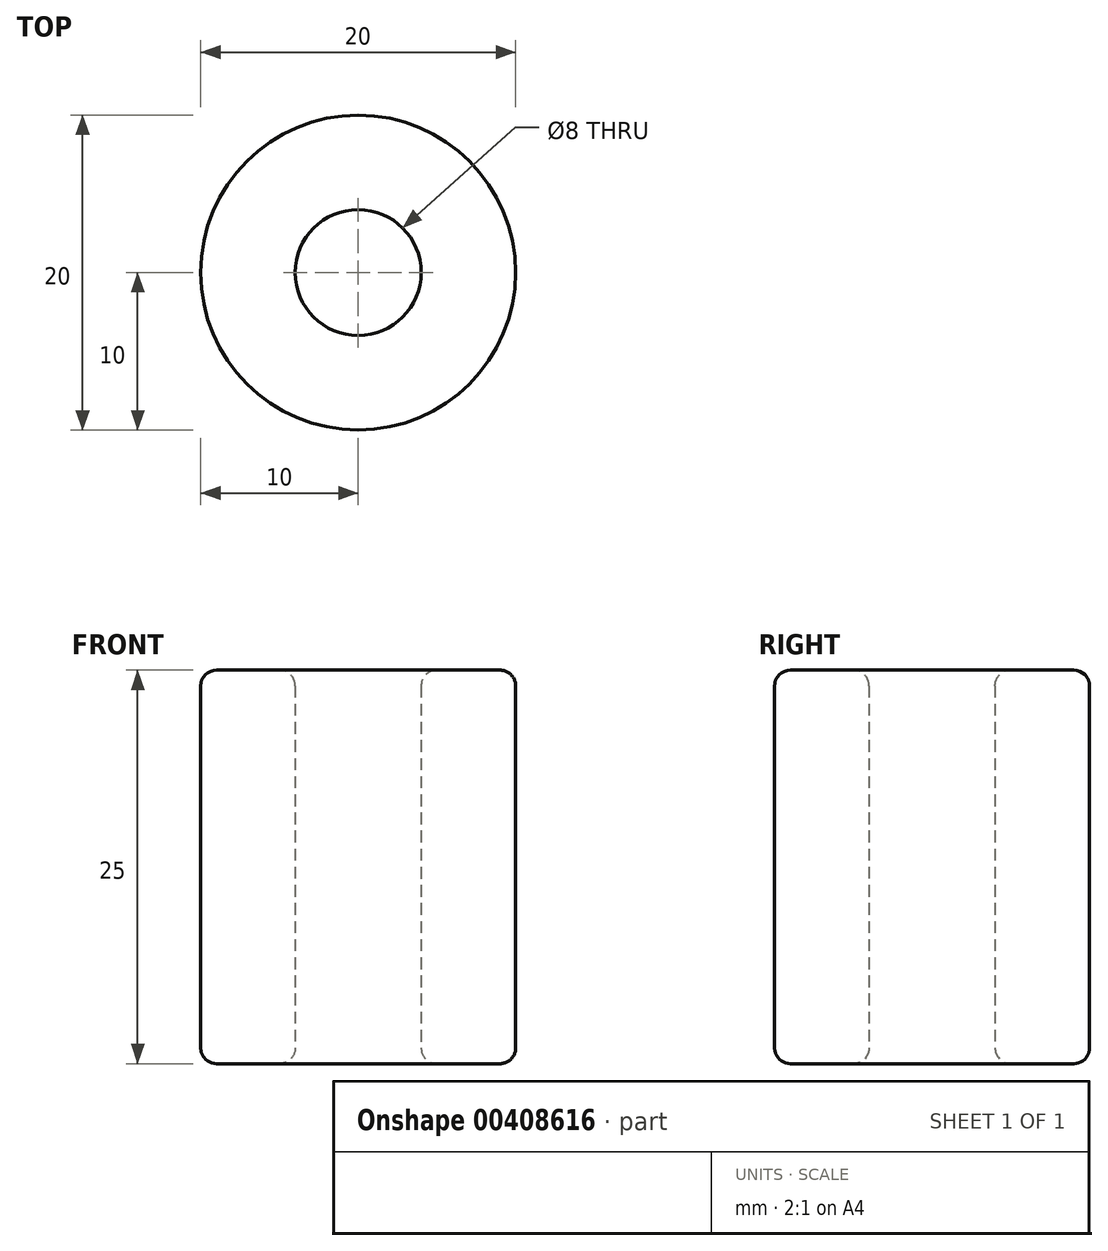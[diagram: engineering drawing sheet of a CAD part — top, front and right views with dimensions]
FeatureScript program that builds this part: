
annotation { "Feature Type Name" : "Feature", "Feature Type Description" : "" }
export const myFeature = defineFeature(function(context is Context, id is Id, definition is map)
    precondition{}
    {
        {
            var Q0;
            Q0=qCreatedBy(makeId("Top.planeOp"),FACE);
            var sketch = newSketch(context, id + "F0", { "sketchPlane" : qUnion([Q0])});
            skCircle(sketch, "E0", {"center": v(0, 0) * mm, "radius": 10 * mm});
            skCircle(sketch, "E1", {"center": v(0, 0) * mm, "radius": 4 * mm});
            skSolve(sketch);
        }
        {
            var Q0;
            Q0 = qSketchRegion(id + "F0", true);
            extrude(context, id + "F1", {"entities" : qUnion([Q0]), "depth" : 25 * mm});
        }
        {
            var Q0;
            Q0=makeQuery(id+"F1.opExtrude","SWEPT_FACE",FACE,{"disambiguationData":[OSD([sQuery(id+"F0.wireOp",EDGE,"E0")])]});
            var Q1;
            Q1=makeQuery(id+"F1.opExtrude","SWEPT_FACE",FACE,{"disambiguationData":[OSD([sQuery(id+"F0.wireOp",EDGE,"E1")])]});
            fillet(context, id + "F2", {"entities" : qUnion([Q0, Q1]), "radius" : 1 * mm, "tangentPropagation" : true, "allowEdgeOverflow" : false});
        }
    });
